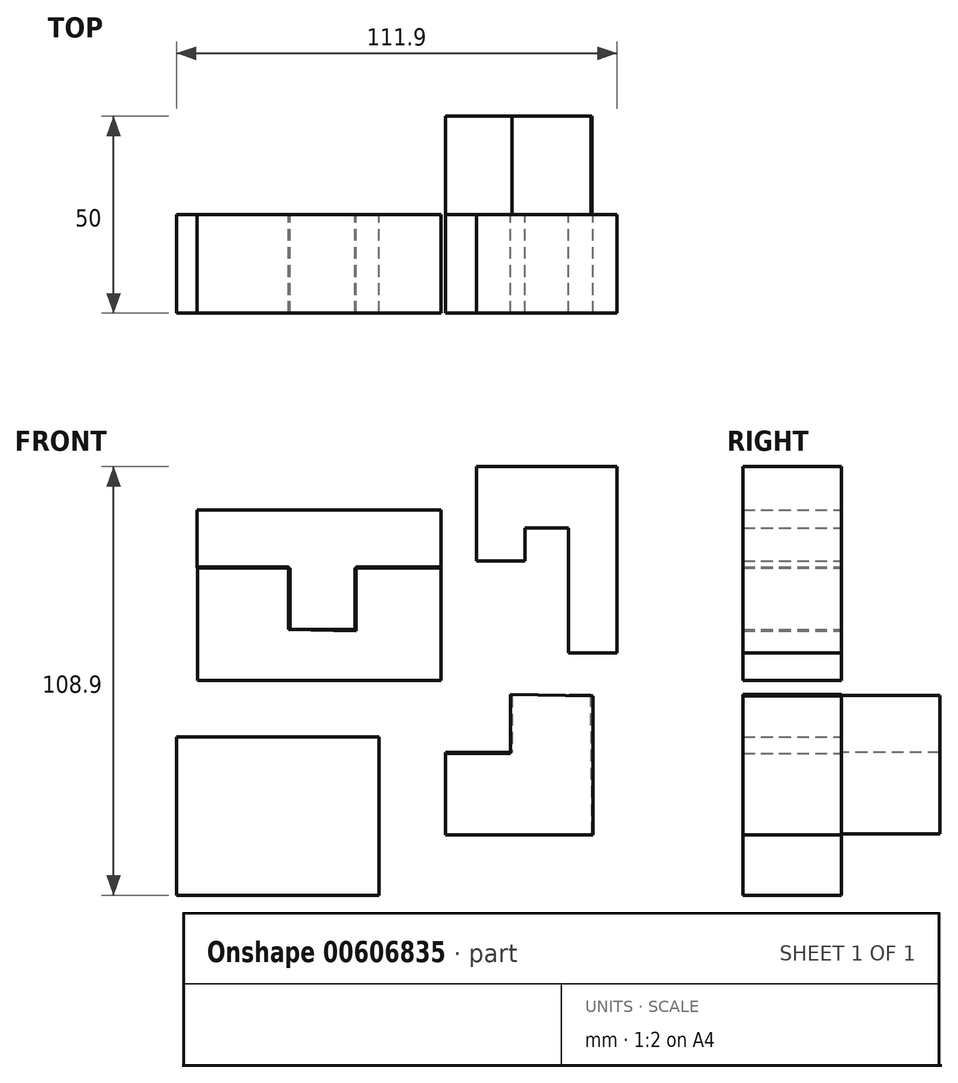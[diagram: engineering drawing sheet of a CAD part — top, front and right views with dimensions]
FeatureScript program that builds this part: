
annotation { "Feature Type Name" : "Feature", "Feature Type Description" : "" }
export const myFeature = defineFeature(function(context is Context, id is Id, definition is map)
    precondition{}
    {
        {
            var Q0;
            Q0=qCreatedBy(makeId("Front.planeOp"),FACE);
            var sketch = newSketch(context, id + "F0", { "sketchPlane" : qUnion([Q0])});
            skLineSegment(sketch, "E0", {"start": v(-46.05, 32.7) * mm, "end": v(-30.75, 32.7) * mm});
            skLineSegment(sketch, "E1", {"start": v(-46.05, 32.7) * mm, "end": v(-46.05, 3.9) * mm});
            skLineSegment(sketch, "E2", {"start": v(-46.05, 3.9) * mm, "end": v(15.75, 3.9) * mm});
            skLineSegment(sketch, "E3", {"start": v(15.75, 3.9) * mm, "end": v(15.75, 32.7) * mm});
            skLineSegment(sketch, "E4", {"start": v(15.75, 32.7) * mm, "end": v(-5.85, 32.7) * mm});
            skLineSegment(sketch, "E5", {"start": v(-5.85, 32.7) * mm, "end": v(-5.85, 16.5) * mm});
            skLineSegment(sketch, "E6", {"start": v(-30.75, 32.7) * mm, "end": v(-22.95, 32.7) * mm});
            skLineSegment(sketch, "E7", {"start": v(-22.95, 32.7) * mm, "end": v(-22.95, 16.8) * mm});
            skLineSegment(sketch, "E8", {"start": v(-22.95, 16.8) * mm, "end": v(-5.85, 16.5) * mm});
            skSolve(sketch);
        }
        {
            var Q0;
            Q0 = qSketchRegion(id + "F0", true);
            extrude(context, id + "F1", {"entities" : qUnion([Q0]), "depth" : 25 * mm, "offsetDistance" : 25 * mm});
        }
        {
            var Q0;
            Q0=qCreatedBy(makeId("Front.planeOp"),FACE);
            var sketch = newSketch(context, id + "F2", { "sketchPlane" : qUnion([Q0])});
            skLineSegment(sketch, "E9", {"start": v(-22.65, 16.8) * mm, "end": v(-6.15, 16.8) * mm});
            skLineSegment(sketch, "E10", {"start": v(-6.15, 16.8) * mm, "end": v(-6.15, 32.4) * mm});
            skLineSegment(sketch, "E11", {"start": v(-6.15, 32.4) * mm, "end": v(15.75, 32.4) * mm});
            skLineSegment(sketch, "E12", {"start": v(15.75, 32.4) * mm, "end": v(15.75, 47.12) * mm});
            skLineSegment(sketch, "E13", {"start": v(15.75, 47.12) * mm, "end": v(-46.2, 47.12) * mm});
            skLineSegment(sketch, "E14", {"start": v(-46.2, 47.12) * mm, "end": v(-46.2, 32.4) * mm});
            skLineSegment(sketch, "E15", {"start": v(-46.2, 32.4) * mm, "end": v(-22.65, 32.4) * mm});
            skLineSegment(sketch, "E16", {"start": v(-22.65, 32.4) * mm, "end": v(-22.65, 16.8) * mm});
            skSolve(sketch);
        }
        {
            var Q0;
            Q0 = qSketchRegion(id + "F2", true);
            extrude(context, id + "F3", {"entities" : qUnion([Q0]), "depth" : 25 * mm, "offsetDistance" : 25 * mm});
        }
        {
            var Q0;
            Q0=qCreatedBy(makeId("Front.planeOp"),FACE);
            var sketch = newSketch(context, id + "F4", { "sketchPlane" : qUnion([Q0])});
            skLineSegment(sketch, "E17", {"start": v(-51.45, -10.5) * mm, "end": v(0, -10.5) * mm});
            skLineSegment(sketch, "E18", {"start": v(0, -10.5) * mm, "end": v(0, -50.7) * mm});
            skLineSegment(sketch, "E19", {"start": v(0, -50.7) * mm, "end": v(-51.45, -50.7) * mm});
            skLineSegment(sketch, "E20", {"start": v(-51.45, -50.7) * mm, "end": v(-51.45, -10.5) * mm});
            skSolve(sketch);
        }
        {
            var Q0;
            Q0 = qSketchRegion(id + "F4", true);
            extrude(context, id + "F5", {"entities" : qUnion([Q0]), "depth" : 25 * mm, "offsetDistance" : 25 * mm});
        }
        {
            var Q0;
            Q0=qCreatedBy(makeId("Front.planeOp"),FACE);
            var sketch = newSketch(context, id + "F6", { "sketchPlane" : qUnion([Q0])});
            skLineSegment(sketch, "E21", {"start": v(54.3, -0.11) * mm, "end": v(54.3, -35.4) * mm});
            skLineSegment(sketch, "E22", {"start": v(54.3, -35.4) * mm, "end": v(16.95, -35.4) * mm});
            skLineSegment(sketch, "E23", {"start": v(16.95, -35.4) * mm, "end": v(16.95, -14.7) * mm});
            skLineSegment(sketch, "E24", {"start": v(16.95, -14.7) * mm, "end": v(33.45, -14.7) * mm});
            skLineSegment(sketch, "E25", {"start": v(33.45, -14.7) * mm, "end": v(33.45, 0.28) * mm});
            skLineSegment(sketch, "E26", {"start": v(33.45, 0.28) * mm, "end": v(54.3, -0.11) * mm});
            skSolve(sketch);
        }
        {
            var Q0;
            Q0 = qSketchRegion(id + "F6", true);
            extrude(context, id + "F7", {"entities" : qUnion([Q0]), "depth" : 25 * mm, "offsetDistance" : 25 * mm});
        }
        {
            var Q0;
            Q0 = qSketchRegion(id + "F6", true);
            extrude(context, id + "F8", {"entities" : qUnion([Q0]), "operationType" : NewBodyOperationType.ADD, "depth" : 25 * mm, "offsetDistance" : 25 * mm});
        }
        {
            var Q0;
            Q0=qCreatedBy(makeId("Front.planeOp"),FACE);
            var sketch = newSketch(context, id + "F9", { "sketchPlane" : qUnion([Q0])});
            skLineSegment(sketch, "E27", {"start": v(53.85, 0) * mm, "end": v(33.75, 0) * mm});
            skLineSegment(sketch, "E28", {"start": v(33.75, 0) * mm, "end": v(33.75, -14.4) * mm});
            skLineSegment(sketch, "E29", {"start": v(33.75, -14.4) * mm, "end": v(16.95, -14.4) * mm});
            skLineSegment(sketch, "E30", {"start": v(16.95, -14.4) * mm, "end": v(16.95, -35.1) * mm});
            skLineSegment(sketch, "E31", {"start": v(16.95, -35.1) * mm, "end": v(54.15, -35.1) * mm});
            skLineSegment(sketch, "E32", {"start": v(54.15, -35.1) * mm, "end": v(53.85, 0) * mm});
            skSolve(sketch);
        }
        {
            var Q0;
            Q0 = qSketchRegion(id + "F9", true);
            extrude(context, id + "F10", {"entities" : qUnion([Q0]), "operationType" : NewBodyOperationType.ADD, "oppositeDirection" : true, "depth" : 25 * mm, "offsetDistance" : 25 * mm});
        }
        {
            var Q0;
            Q0=qCreatedBy(makeId("Front.planeOp"),FACE);
            var sketch = newSketch(context, id + "F11", { "sketchPlane" : qUnion([Q0])});
            skLineSegment(sketch, "E33", {"start": v(24.75, 34.2) * mm, "end": v(24.75, 58.2) * mm});
            skLineSegment(sketch, "E34", {"start": v(24.75, 58.2) * mm, "end": v(60.45, 58.2) * mm});
            skLineSegment(sketch, "E35", {"start": v(60.45, 58.2) * mm, "end": v(60.45, 10.8) * mm});
            skLineSegment(sketch, "E36", {"start": v(60.45, 10.8) * mm, "end": v(48.15, 10.8) * mm});
            skLineSegment(sketch, "E37", {"start": v(48.15, 10.8) * mm, "end": v(48.15, 42.6) * mm});
            skLineSegment(sketch, "E38", {"start": v(48.15, 42.6) * mm, "end": v(37.05, 42.6) * mm});
            skLineSegment(sketch, "E39", {"start": v(37.05, 42.6) * mm, "end": v(37.05, 34.2) * mm});
            skLineSegment(sketch, "E40", {"start": v(37.05, 34.2) * mm, "end": v(24.75, 34.2) * mm});
            skSolve(sketch);
        }
        {
            var Q0;
            Q0 = qSketchRegion(id + "F11", true);
            extrude(context, id + "F12", {"entities" : qUnion([Q0]), "depth" : 25 * mm, "offsetDistance" : 25 * mm});
        }
    });
